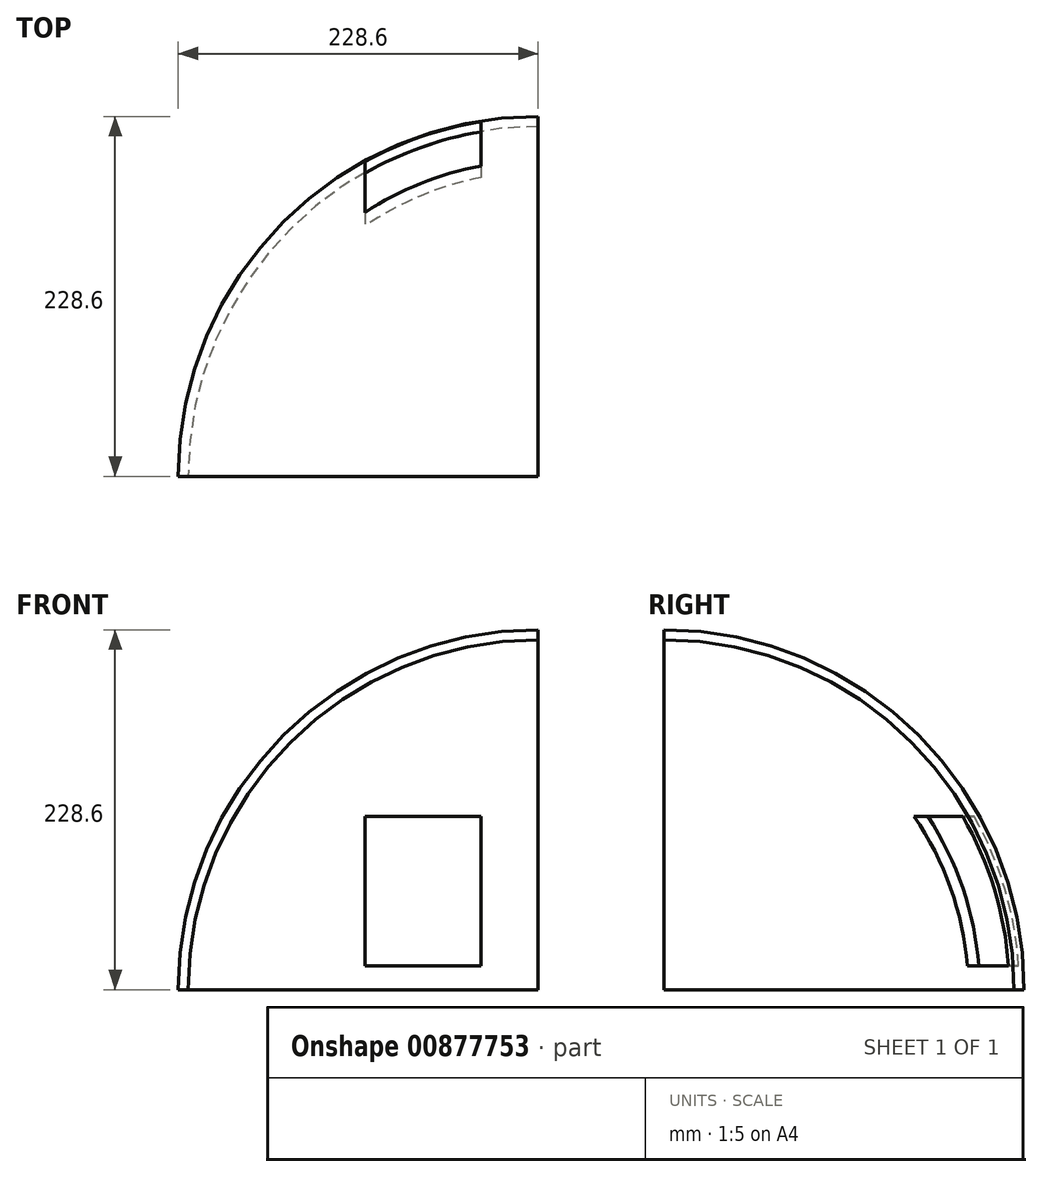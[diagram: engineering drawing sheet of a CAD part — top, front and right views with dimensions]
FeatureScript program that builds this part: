
annotation { "Feature Type Name" : "Feature", "Feature Type Description" : "" }
export const myFeature = defineFeature(function(context is Context, id is Id, definition is map)
    precondition{}
    {
        {
            var Q0;
            Q0=qCreatedBy(makeId("Front.planeOp"),FACE);
            var sketch = newSketch(context, id + "F0", { "sketchPlane" : qUnion([Q0])});
            skArc(sketch, "E0", {"start": v(0, 228.6) * mm, "mid": v(-161.64, 161.64) * mm, "end": v(-228.6, 0) * mm});
            skLineSegment(sketch, "E1", {"start": v(-228.6, 0) * mm, "end": v(0, 0) * mm});
            skLineSegment(sketch, "E2", {"start": v(0, 228.6) * mm, "end": v(0, 0) * mm});
            skArc(sketch, "E3", {"start": v(0, 222.25) * mm, "mid": v(-157.15, 157.15) * mm, "end": v(-222.25, 0) * mm});
            skLineSegment(sketch, "E4", {"start": v(0, 222.25) * mm, "end": v(0, 0) * mm});
            skLineSegment(sketch, "E5", {"start": v(0, 0) * mm, "end": v(-222.25, 0) * mm});
            skSolve(sketch);
        }
        {
            var Q0;
            Q0=makeQuery(id+"F0.imprint","IMPRINT",FACE,{"disambiguationData":[TD([[makeQuery(id+"F0.imprint","IMPRINT",EDGE,{"derivedFrom":sQuery(id+"F0.wireOp",EDGE,"E0")}),1.0]])]});
            var Q1;
            Q1=sQuery(id+"F0.wireOp",EDGE,"E2");
            revolve(context, id + "F1", {"surfaceOperationType" : NewSurfaceOperationType.NEW, "entities" : qUnion([Q0]), "axis" : qUnion([Q1]), "revolveType" : RevolveType.ONE_DIRECTION, "angle" : 90 * degree});
        }
        {
            var Q0;
            Q0=qCreatedBy(makeId("Front.planeOp"),FACE);
            var sketch = newSketch(context, id + "F2", { "sketchPlane" : qUnion([Q0])});
            skLineSegment(sketch, "E6.bottom", {"start": v(-110, 15.1) * mm, "end": v(-36.4, 15.1) * mm});
            skLineSegment(sketch, "E6.top", {"start": v(-110, 109.9) * mm, "end": v(-36.4, 109.9) * mm});
            skLineSegment(sketch, "E6.left", {"start": v(-110, 15.1) * mm, "end": v(-110, 109.9) * mm});
            skLineSegment(sketch, "E6.right", {"start": v(-36.4, 15.1) * mm, "end": v(-36.4, 109.9) * mm});
            skSolve(sketch);
        }
        {
            var Q0;
            Q0 = qSketchRegion(id + "F2", true);
            extrude(context, id + "F3", {"entities" : qUnion([Q0]), "operationType" : NewBodyOperationType.REMOVE, "oppositeDirection" : true, "depth" : 285.24 * mm, "offsetDistance" : 25.4 * mm});
        }
    });
